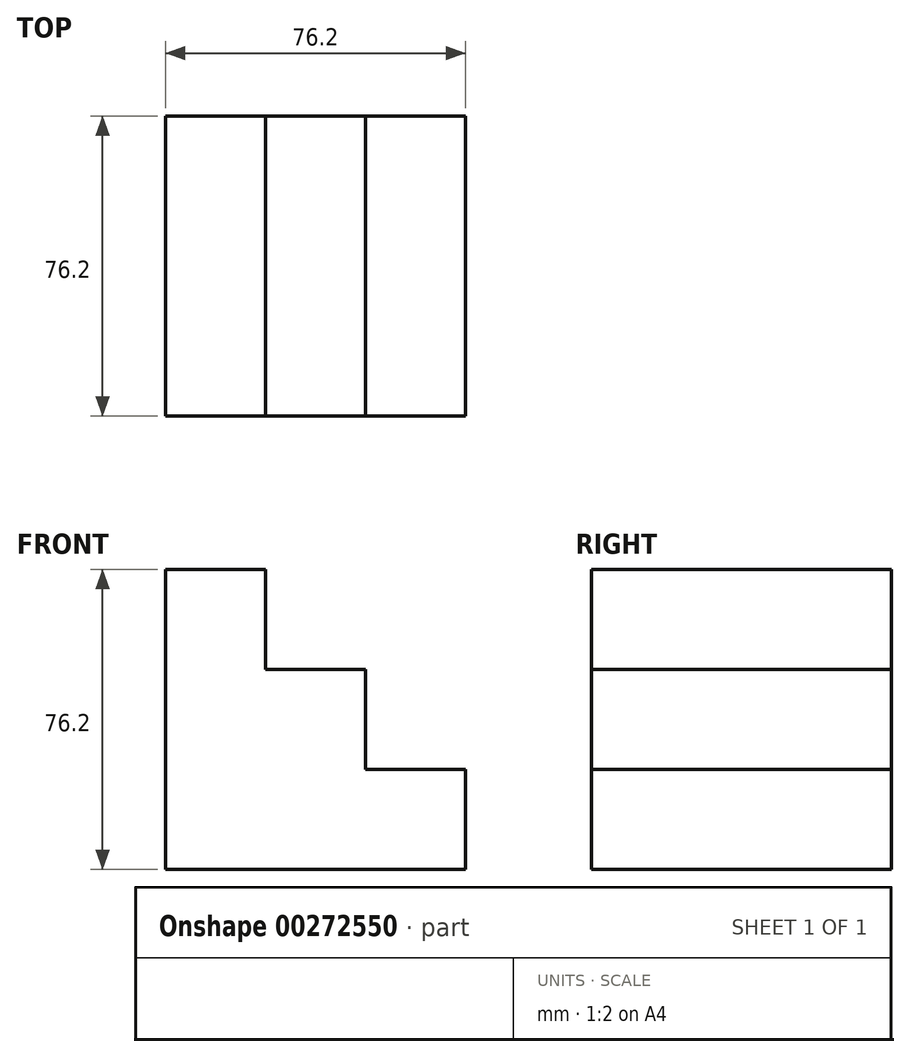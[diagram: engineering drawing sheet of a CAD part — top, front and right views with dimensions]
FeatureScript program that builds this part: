
annotation { "Feature Type Name" : "Feature", "Feature Type Description" : "" }
export const myFeature = defineFeature(function(context is Context, id is Id, definition is map)
    precondition{}
    {
        {
            var Q0;
            Q0=qCreatedBy(makeId("Front.planeOp"),FACE);
            var sketch = newSketch(context, id + "F0", { "sketchPlane" : qUnion([Q0])});
            skLineSegment(sketch, "E0", {"start": v(0, 0) * mm, "end": v(0, 76.2) * mm});
            skLineSegment(sketch, "E1", {"start": v(0, 76.2) * mm, "end": v(25.4, 76.2) * mm});
            skLineSegment(sketch, "E2", {"start": v(25.4, 76.2) * mm, "end": v(25.4, 50.8) * mm});
            skLineSegment(sketch, "E3", {"start": v(25.4, 50.8) * mm, "end": v(50.8, 50.8) * mm});
            skLineSegment(sketch, "E4", {"start": v(50.8, 50.8) * mm, "end": v(50.8, 25.4) * mm});
            skLineSegment(sketch, "E5", {"start": v(50.8, 25.4) * mm, "end": v(76.2, 25.4) * mm});
            skLineSegment(sketch, "E6", {"start": v(76.2, 25.4) * mm, "end": v(76.2, 0) * mm});
            skLineSegment(sketch, "E7", {"start": v(76.2, 0) * mm, "end": v(0, 0) * mm});
            skSolve(sketch);
        }
        {
            var Q0;
            Q0 = qSketchRegion(id + "F0", true);
            extrude(context, id + "F1", {"entities" : qUnion([Q0]), "depth" : 76.2 * mm});
        }
    });
